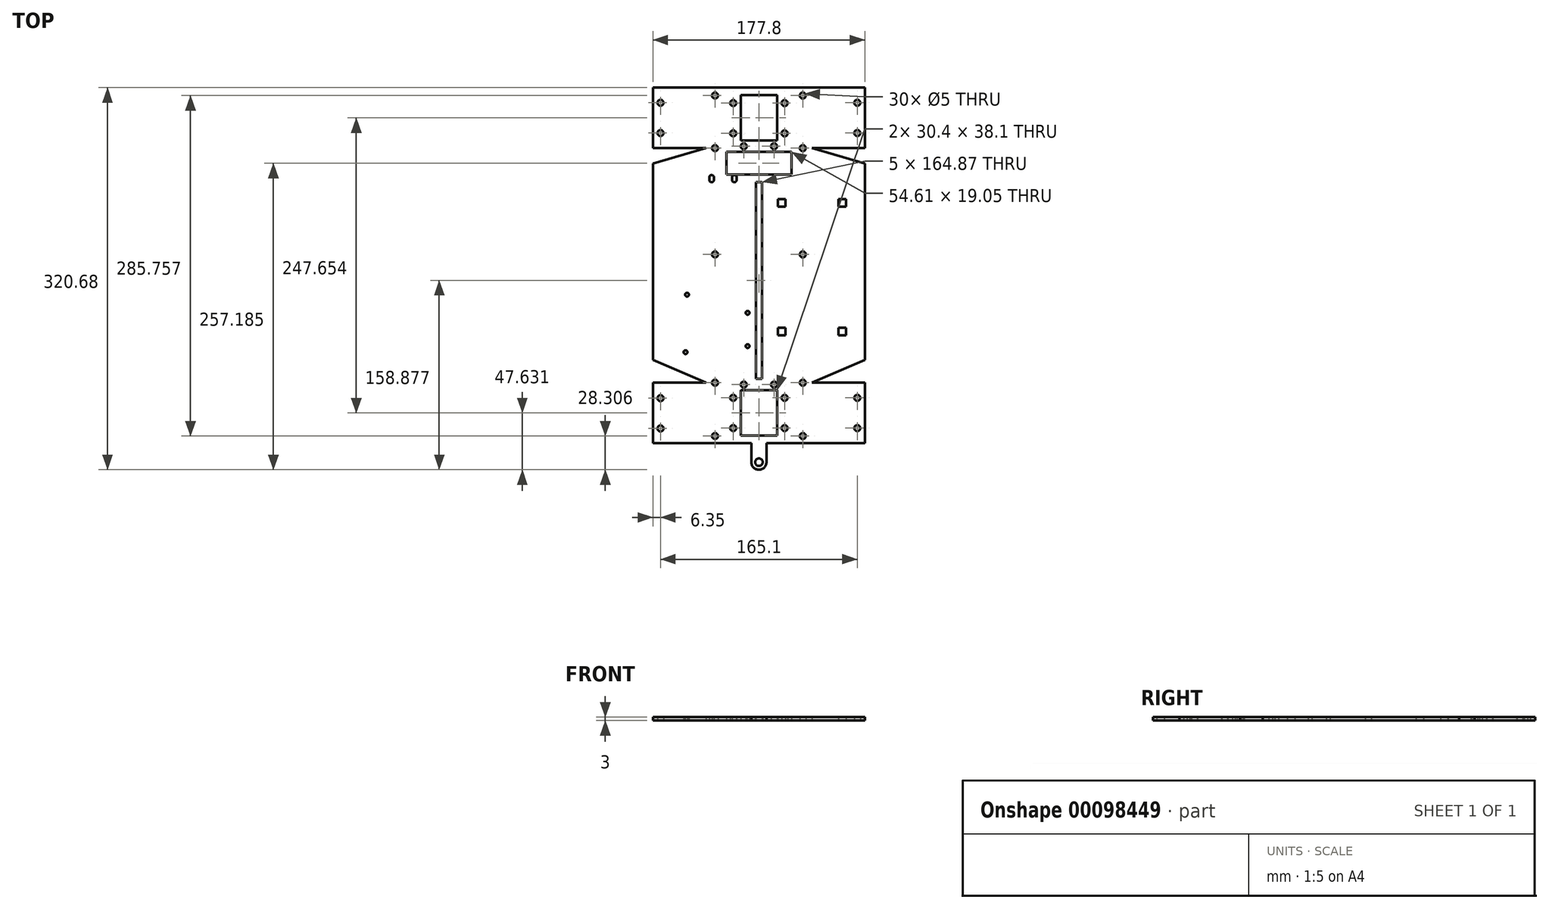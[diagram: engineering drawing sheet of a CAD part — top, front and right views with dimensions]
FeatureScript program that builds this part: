
annotation { "Feature Type Name" : "Feature", "Feature Type Description" : "" }
export const myFeature = defineFeature(function(context is Context, id is Id, definition is map)
    precondition{}
    {
        {
            var Q0;
            Q0=qCreatedBy(makeId("Top.planeOp"),FACE);
            var sketch = newSketch(context, id + "F0", { "sketchPlane" : qUnion([Q0])});
            skLineSegment(sketch, "E0.bottom", {"start": v(88.9, 89.17) * mm, "end": v(44.45, 89.17) * mm});
            skLineSegment(sketch, "E0.left", {"start": v(88.9, 76.2) * mm, "end": v(88.9, 66.95) * mm});
            skLineSegment(sketch, "E0.right", {"start": v(-88.9, 76.2) * mm, "end": v(-88.9, -88.63) * mm});
            skLineSegment(sketch, "E1.bottom", {"start": v(27.3, 86) * mm, "end": v(-27.3, 86) * mm});
            skLineSegment(sketch, "E1.top", {"start": v(27.3, 66.95) * mm, "end": v(-27.3, 66.95) * mm});
            skLineSegment(sketch, "E1.left", {"start": v(27.3, 86) * mm, "end": v(27.3, 66.95) * mm});
            skLineSegment(sketch, "E1.right", {"start": v(-27.3, 86) * mm, "end": v(-27.3, 66.95) * mm});
            skArc(sketch, "E2", {"start": v(-37.7, 64.64) * mm, "mid": v(-39.69, 66.63) * mm, "end": v(-41.67, 64.64) * mm});
            skArc(sketch, "E3", {"start": v(-41.67, 62.61) * mm, "mid": v(-39.69, 60.63) * mm, "end": v(-37.7, 62.61) * mm});
            skLineSegment(sketch, "E4", {"start": v(-41.67, 64.64) * mm, "end": v(-41.67, 62.61) * mm});
            skLineSegment(sketch, "E5.MirrorCS", {"start": v(-37.7, 64.64) * mm, "end": v(-37.7, 62.61) * mm});
            skArc(sketch, "E6.MirrorCS", {"start": v(-22.62, 64.64) * mm, "mid": v(-20.64, 66.63) * mm, "end": v(-18.65, 64.64) * mm});
            skLineSegment(sketch, "E7.MirrorCS", {"start": v(-22.62, 64.64) * mm, "end": v(-22.62, 62.61) * mm});
            skLineSegment(sketch, "E8.MirrorCS", {"start": v(-18.65, 64.64) * mm, "end": v(-18.65, 62.61) * mm});
            skArc(sketch, "E9.MirrorCS", {"start": v(-18.65, 62.61) * mm, "mid": v(-20.64, 60.63) * mm, "end": v(-22.62, 62.61) * mm});
            skLineSegment(sketch, "E10", {"start": v(88.9, 66.95) * mm, "end": v(88.9, -88.63) * mm});
            skLineSegment(sketch, "E11.bottom", {"start": v(88.9, 139.97) * mm, "end": v(-88.9, 139.97) * mm});
            skLineSegment(sketch, "E11.left", {"start": v(88.9, 139.97) * mm, "end": v(88.9, 89.17) * mm});
            skLineSegment(sketch, "E11.right", {"start": v(-88.9, 139.97) * mm, "end": v(-88.9, 89.17) * mm});
            skPoint(sketch, "E11.middle", {"position": v(0, 114.57) * mm});
            skLineSegment(sketch, "E12.bottom", {"start": v(15.2, 133.62) * mm, "end": v(-15.2, 133.62) * mm});
            skLineSegment(sketch, "E12.top", {"start": v(15.2, 95.52) * mm, "end": v(-15.2, 95.52) * mm});
            skCircle(sketch, "E13", {"center": v(-82.55, 127.27) * mm, "radius": 2.5 * mm});
            skCircle(sketch, "E14.MirrorC", {"center": v(-82.55, 101.87) * mm, "radius": 2.5 * mm});
            skCircle(sketch, "E15.MirrorC", {"center": v(82.55, 127.27) * mm, "radius": 2.5 * mm});
            skCircle(sketch, "E16.MirrorC", {"center": v(82.55, 101.87) * mm, "radius": 2.5 * mm});
            skCircle(sketch, "E17", {"center": v(-12.7, 90.76) * mm, "radius": 2.5 * mm});
            skCircle(sketch, "E18.MirrorC", {"center": v(12.7, 90.76) * mm, "radius": 2.5 * mm});
            skPoint(sketch, "E19", {"position": v(-44.45, 89.17) * mm});
            skLineSegment(sketch, "E20", {"start": v(-88.9, 76.2) * mm, "end": v(-44.45, 89.17) * mm});
            skLineSegment(sketch, "E21.MirrorCS", {"start": v(88.9, 76.2) * mm, "end": v(44.45, 89.17) * mm});
            skPoint(sketch, "E22", {"position": v(-88.9, -107.68) * mm});
            skPoint(sketch, "E23", {"position": v(-44.45, -107.68) * mm});
            skLineSegment(sketch, "E24", {"start": v(-88.9, -88.63) * mm, "end": v(-44.45, -107.68) * mm});
            skLineSegment(sketch, "E25.MirrorCS", {"start": v(88.9, -88.63) * mm, "end": v(44.45, -107.68) * mm});
            skLineSegment(sketch, "E26", {"start": v(88.9, -107.68) * mm, "end": v(44.45, -107.68) * mm});
            skLineSegment(sketch, "E27", {"start": v(-88.9, -107.68) * mm, "end": v(-88.9, -158.48) * mm});
            skLineSegment(sketch, "E28", {"start": v(-88.9, -158.48) * mm, "end": v(-6.35, -158.48) * mm});
            skLineSegment(sketch, "E29", {"start": v(88.9, -158.48) * mm, "end": v(88.9, -107.68) * mm});
            skPoint(sketch, "E30", {"position": v(0, -133.08) * mm});
            skLineSegment(sketch, "E31.bottom", {"start": v(15.2, -152.13) * mm, "end": v(-15.2, -152.13) * mm});
            skLineSegment(sketch, "E31.top", {"start": v(15.2, -114.03) * mm, "end": v(-15.2, -114.03) * mm});
            skCircle(sketch, "E32", {"center": v(82.55, -120.38) * mm, "radius": 2.5 * mm});
            skCircle(sketch, "E33.MirrorC", {"center": v(82.55, -145.78) * mm, "radius": 2.5 * mm});
            skCircle(sketch, "E34.MirrorC", {"center": v(-82.55, -120.65) * mm, "radius": 2.5 * mm});
            skCircle(sketch, "E35.MirrorC", {"center": v(-82.55, -146.05) * mm, "radius": 2.5 * mm});
            skCircle(sketch, "E36", {"center": v(12.7, -109.27) * mm, "radius": 2.5 * mm});
            skCircle(sketch, "E37.MirrorC", {"center": v(-12.7, -109.27) * mm, "radius": 2.5 * mm});
            skCircle(sketch, "E38", {"center": v(0, -174.36) * mm, "radius": 3.18 * mm});
            skLineSegment(sketch, "E39", {"start": v(0, -180.7) * mm, "end": v(0, -180.7) * mm});
            skLineSegment(sketch, "E40", {"start": v(-6.35, -174.36) * mm, "end": v(-6.35, -158.48) * mm});
            skLineSegment(sketch, "E41.MirrorCS", {"start": v(6.35, -174.36) * mm, "end": v(6.35, -158.48) * mm});
            skArc(sketch, "E42.filletArc", {"start": v(-6.35, -174.36) * mm, "mid": v(-4.5, -178.85) * mm, "end": v(0, -180.7) * mm});
            skArc(sketch, "E43.MirrorCS", {"start": v(6.35, -174.36) * mm, "mid": v(4.5, -178.85) * mm, "end": v(0, -180.7) * mm});
            skPoint(sketch, "E44.MirrorCS.start.orphan", {"position": v(0, -180.7) * mm});
            skCircle(sketch, "E45", {"center": v(-60.33, -33.76) * mm, "radius": 1.59 * mm});
            skCircle(sketch, "E46", {"center": v(-61.6, -82.02) * mm, "radius": 1.59 * mm});
            skCircle(sketch, "E47", {"center": v(-9.53, -76.94) * mm, "radius": 1.59 * mm});
            skCircle(sketch, "E48", {"center": v(-9.53, -49) * mm, "radius": 1.59 * mm});
            skLineSegment(sketch, "E49.bottom", {"start": v(2.5, 60.6) * mm, "end": v(-2.5, 60.6) * mm});
            skLineSegment(sketch, "E49.top", {"start": v(2.5, -104.27) * mm, "end": v(-2.5, -104.27) * mm});
            skLineSegment(sketch, "E49.left", {"start": v(2.5, 60.6) * mm, "end": v(2.5, -104.27) * mm});
            skLineSegment(sketch, "E49.right", {"start": v(-2.5, 60.6) * mm, "end": v(-2.5, -104.27) * mm});
            skLineSegment(sketch, "E50", {"start": v(-15.2, 95.52) * mm, "end": v(-15.2, 133.62) * mm});
            skLineSegment(sketch, "E51.MirrorCS", {"start": v(15.2, 95.52) * mm, "end": v(15.2, 133.62) * mm});
            skLineSegment(sketch, "E52", {"start": v(-15.2, -114.03) * mm, "end": v(-15.2, -152.13) * mm});
            skLineSegment(sketch, "E53", {"start": v(15.2, -114.03) * mm, "end": v(15.2, -152.13) * mm});
            skCircle(sketch, "E54", {"center": v(-21.55, 127) * mm, "radius": 2.5 * mm});
            skCircle(sketch, "E55", {"center": v(-21.55, 101.6) * mm, "radius": 2.5 * mm});
            skCircle(sketch, "E56.MirrorC", {"center": v(21.55, 127) * mm, "radius": 2.5 * mm});
            skCircle(sketch, "E57.MirrorC", {"center": v(21.55, 101.6) * mm, "radius": 2.5 * mm});
            skCircle(sketch, "E58", {"center": v(21.55, -120.38) * mm, "radius": 2.5 * mm});
            skCircle(sketch, "E59", {"center": v(21.55, -145.78) * mm, "radius": 2.5 * mm});
            skCircle(sketch, "E60.MirrorC", {"center": v(-21.55, -120.38) * mm, "radius": 2.5 * mm});
            skCircle(sketch, "E61.MirrorC", {"center": v(-21.55, -145.78) * mm, "radius": 2.5 * mm});
            skCircle(sketch, "E62", {"center": v(-36.8, 89.17) * mm, "radius": 2.5 * mm});
            skCircle(sketch, "E63", {"center": v(-36.8, -107.68) * mm, "radius": 2.5 * mm});
            skCircle(sketch, "E64", {"center": v(-36.8, 133.35) * mm, "radius": 2.5 * mm});
            skCircle(sketch, "E65", {"center": v(-36.8, -152.4) * mm, "radius": 2.5 * mm});
            skCircle(sketch, "E66", {"center": v(-36.8, 0) * mm, "radius": 2.5 * mm});
            skCircle(sketch, "E67.MirrorC", {"center": v(36.8, 0) * mm, "radius": 2.5 * mm});
            skCircle(sketch, "E68.MirrorC", {"center": v(36.8, -107.68) * mm, "radius": 2.5 * mm});
            skCircle(sketch, "E69.MirrorC", {"center": v(36.8, -152.4) * mm, "radius": 2.5 * mm});
            skCircle(sketch, "E70.MirrorC", {"center": v(36.8, 133.35) * mm, "radius": 2.5 * mm});
            skCircle(sketch, "E71.MirrorC", {"center": v(36.8, 89.17) * mm, "radius": 2.5 * mm});
            skLineSegment(sketch, "E72.bottom", {"start": v(22.22, 46.3) * mm, "end": v(15.87, 46.3) * mm});
            skLineSegment(sketch, "E72.top", {"start": v(22.22, 39.96) * mm, "end": v(15.87, 39.96) * mm});
            skLineSegment(sketch, "E72.left", {"start": v(22.22, 46.3) * mm, "end": v(22.22, 39.96) * mm});
            skLineSegment(sketch, "E72.right", {"start": v(15.87, 46.3) * mm, "end": v(15.87, 39.96) * mm});
            skPoint(sketch, "E72.middle", {"position": v(19.05, 43.13) * mm});
            skLineSegment(sketch, "E73.MirrorCS", {"start": v(66.68, 46.3) * mm, "end": v(73.03, 46.3) * mm});
            skLineSegment(sketch, "E74.MirrorCS", {"start": v(66.68, 46.3) * mm, "end": v(66.68, 39.96) * mm});
            skLineSegment(sketch, "E75.MirrorCS", {"start": v(66.68, 39.96) * mm, "end": v(73.03, 39.96) * mm});
            skLineSegment(sketch, "E76.MirrorCS", {"start": v(73.03, 46.3) * mm, "end": v(73.03, 39.96) * mm});
            skLineSegment(sketch, "E77.MirrorCS", {"start": v(22.22, -61.64) * mm, "end": v(15.87, -61.64) * mm});
            skLineSegment(sketch, "E78.MirrorCS", {"start": v(15.87, -68) * mm, "end": v(15.87, -61.64) * mm});
            skLineSegment(sketch, "E79.MirrorCS", {"start": v(22.22, -68) * mm, "end": v(15.87, -68) * mm});
            skLineSegment(sketch, "E80.MirrorCS", {"start": v(22.22, -68) * mm, "end": v(22.22, -61.64) * mm});
            skLineSegment(sketch, "E81.MirrorCS", {"start": v(66.68, -61.64) * mm, "end": v(73.03, -61.64) * mm});
            skLineSegment(sketch, "E82.MirrorCS", {"start": v(66.68, -68) * mm, "end": v(66.68, -61.64) * mm});
            skLineSegment(sketch, "E83.MirrorCS", {"start": v(66.68, -68) * mm, "end": v(73.03, -68) * mm});
            skLineSegment(sketch, "E84.MirrorCS", {"start": v(73.03, -68) * mm, "end": v(73.03, -61.64) * mm});
            skLineSegment(sketch, "E85.trimOffspring", {"start": v(-44.45, -107.68) * mm, "end": v(-88.9, -107.68) * mm});
            skLineSegment(sketch, "E86.trimOffspring", {"start": v(-44.45, 89.17) * mm, "end": v(-88.9, 89.17) * mm});
            skLineSegment(sketch, "E87.trimOffspring", {"start": v(6.35, -158.48) * mm, "end": v(88.9, -158.48) * mm});
            skSolve(sketch);
        }
        {
            var Q0;
            Q0=makeQuery(id+"F0.imprint","IMPRINT",FACE,{"disambiguationData":[TD([[makeQuery(id+"F0.imprint","IMPRINT",EDGE,{"derivedFrom":sQuery(id+"F0.wireOp",EDGE,"E0.left")}),-1.0]])]});
            extrude(context, id + "F1", {"entities" : qUnion([Q0]), "depth" : 3 * mm});
        }
    });
